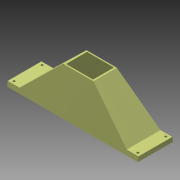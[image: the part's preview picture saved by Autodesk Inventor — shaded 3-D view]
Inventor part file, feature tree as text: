
AUTODESK INVENTOR PART (.ipt)
format: ipt  version: 2015 (Build 190159000, 159)  size: 177,152 bytes
history: native  units: mm
features: sketch x7, extrude x5, plane x1, loft x1, shell x1
ambient origin geometry x8: Origin, YZ Plane, XZ Plane, XY Plane, X Axis, Y Axis, Z Axis, Center Point
bodies: 实体1 (feature_tree)
feature tree (15):
  sketch  "草图1"  dims[d0=2.831305mm d1=500.0mm d2=150.0mm]
  plane  "工作平面1"
  loft  "放样1"
  shell  "抽壳1"  Thickness=150.0mm
  extrude  "拉伸1"  Depth=180.0mm
  extrude  "拉伸2"  TaperAngle=0.0deg  [1 undecoded]
  extrude  "拉伸3"  Depth=5.0mm
  extrude  "拉伸4"  Depth=30.0mm
  extrude  "拉伸5"  Depth=20.0mm TaperAngle=0.0deg
  sketch  "草图2"  dims[d3=180.0mm d4=130.0mm]
  sketch  "草图3"  dims[d5=100.0mm d6=0.0mm d7=90.0deg]
  sketch  "草图4"  dims[d8=0.0mm d9=90.0deg d10=5.0mm]
  sketch  "草图5"  dims[d11=30.0mm d12=30.0mm]
  sketch  "草图6"  dims[d13=20.0mm d14=0.0mm d15=150.0mm d16=0.0mm]
  sketch  "草图7"  dims[d17=150.0mm d18=0.0mm d19=25.0mm d20=25.0mm d21=25.0mm d22=25.0mm d23=15.0mm d24=15.0mm d25=15.0mm d26=15.0mm d27=15.0mm d28=15.0mm d29=15.0mm d30=15.0mm d31=10.0mm d32=0.0mm d33=10.0mm d34=10.0mm d35=10.0mm d36=10.0mm d37=10.0mm d38=0.0mm]
note: 1 required parameter value undecoded (feature->parameter linkage not recoverable at this tier; creation-order binding heuristic only, values carry confidence <= 0.55)
